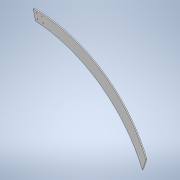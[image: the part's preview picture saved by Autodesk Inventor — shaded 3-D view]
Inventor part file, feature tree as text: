
AUTODESK INVENTOR PART (.ipt)
format: ipt  version: 2020.3 (Build 243373000, 373)  size: 172,544 bytes
history: native  units: mm
features: extrude x6, sketch x6
ambient origin geometry x8: Origin, YZ Plane, XZ Plane, XY Plane, X Axis, Y Axis, Z Axis, Center Point
bodies: Solid1 (feature_tree)
feature tree (12):
  extrude  "Extrusion1"  Depth=40.0mm
  sketch  "Sketch2"  dims[d4=3.490659mm d5=465.0mm]
  extrude  "Extrusion2"  Depth=465.0mm
  extrude  "Extrusion4"  Depth=4.0mm TaperAngle=0.0deg
  extrude  "Extrusion5"  Depth=4.0mm TaperAngle=0.0deg
  extrude  "Extrusion6"  Depth=10.0mm TaperAngle=0.0deg
  extrude  "Extrusion7"  Depth=10.0mm
  sketch  "Sketch1"  dims[d1=30.0mm d2=40.0mm]
  sketch  "Sketch4"  dims[d6=450.0mm d7=4.0mm d8=0.0mm]
  sketch  "Sketch5"  dims[d9=90.0mm d10=4.0mm d11=0.0mm]
  sketch  "Sketch6"  dims[d16=3.490659mm d17=10.0mm d18=0.0mm]
  sketch  "Sketch7"  dims[d19=10.0mm d20=0.0mm d21=10.0mm d22=700.0mm d23=6.981317mm d24=260.0mm d25=10.0mm d26=0.0mm d27=2.707006mm d28=0.698132mm d29=270.0mm d30=270.0mm d31=3.0mm d32=3.0mm d33=3.0mm d34=3.0mm d35=19.024089mm d36=20.0mm d37=0.0mm d38=0.0mm]
